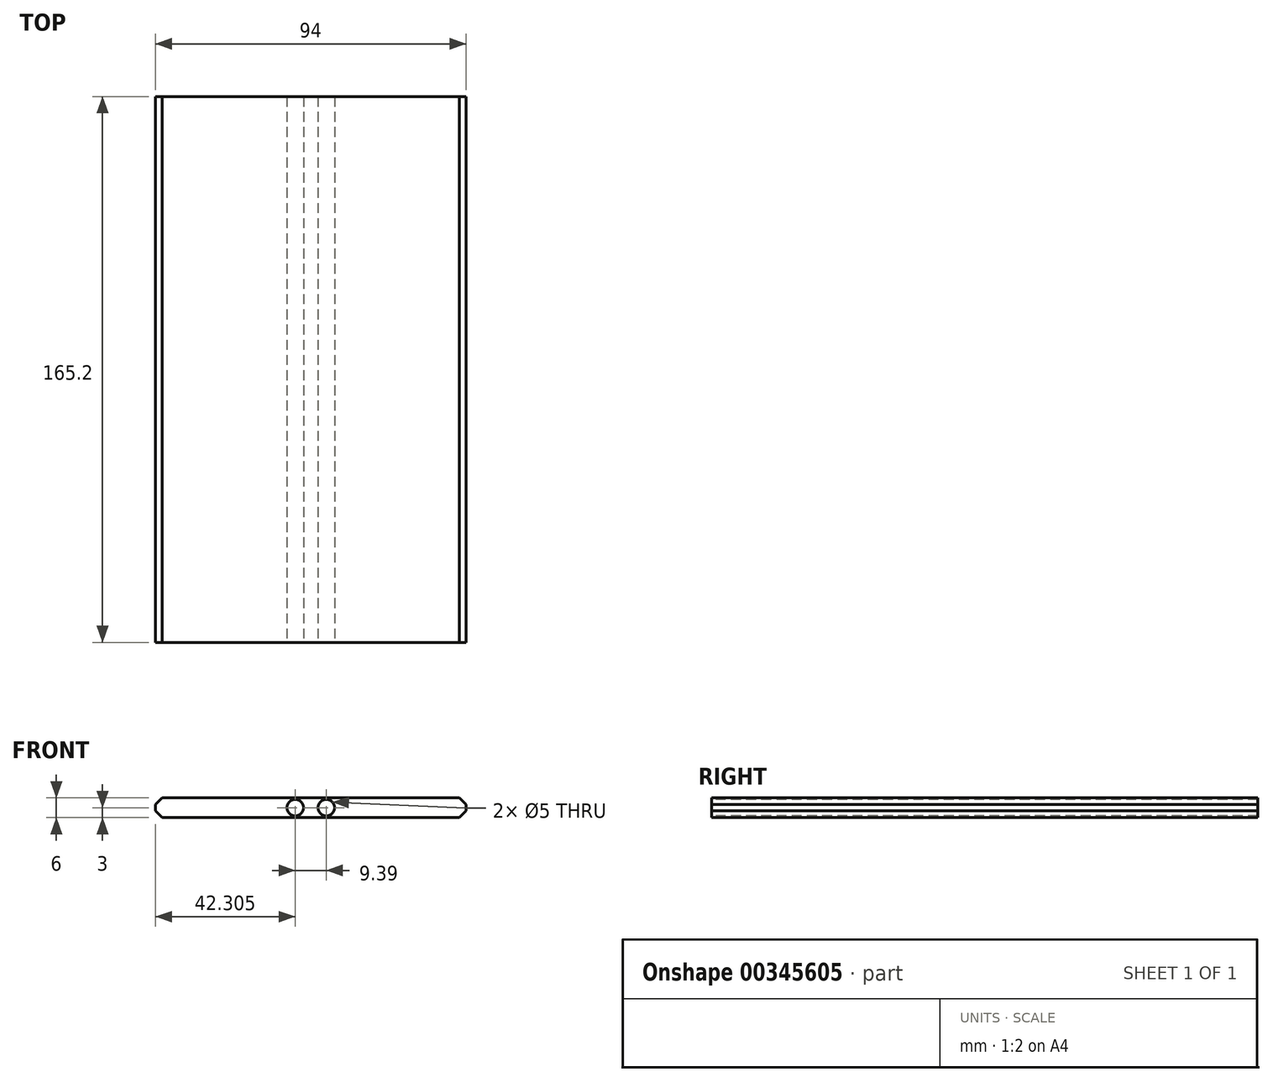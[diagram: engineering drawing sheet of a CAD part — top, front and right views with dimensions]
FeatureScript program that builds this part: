
annotation { "Feature Type Name" : "Feature", "Feature Type Description" : "" }
export const myFeature = defineFeature(function(context is Context, id is Id, definition is map)
    precondition{}
    {
        {
            var Q0;
            Q0=qCreatedBy(makeId("Top.planeOp"),FACE);
            var sketch = newSketch(context, id + "F0", { "sketchPlane" : qUnion([Q0])});
            skLineSegment(sketch, "E0.bottom", {"start": v(0, 0) * mm, "end": v(94, 0) * mm});
            skLineSegment(sketch, "E0.top", {"start": v(0, 165.2) * mm, "end": v(94, 165.2) * mm});
            skLineSegment(sketch, "E0.left", {"start": v(0, 0) * mm, "end": v(0, 165.2) * mm});
            skLineSegment(sketch, "E0.right", {"start": v(94, 0) * mm, "end": v(94, 165.2) * mm});
            skSolve(sketch);
        }
        {
            var Q0;
            Q0=makeQuery(id+"F0.imprint","IMPRINT",FACE,{"disambiguationData":[TD([[makeQuery(id+"F0.imprint","IMPRINT",EDGE,{"derivedFrom":sQuery(id+"F0.wireOp",EDGE,"E0.bottom")}),1.0]])]});
            extrude(context, id + "F1", {"entities" : qUnion([Q0]), "depth" : 6 * mm});
        }
        {
            var Q0;
            Q0=makeQuery(id+"F1.opExtrude","SWEPT_FACE",FACE,{"disambiguationData":[OSD([sQuery(id+"F0.wireOp",EDGE,"E0.bottom")])]});
            var sketch = newSketch(context, id + "F2", { "sketchPlane" : qUnion([Q0])});
            skCircle(sketch, "E1", {"center": v(42.3, 3) * mm, "radius": 2.5 * mm});
            skCircle(sketch, "E2", {"center": v(51.7, 3) * mm, "radius": 2.5 * mm});
            skLineSegment(sketch, "E3", {"start": v(47, 0) * mm, "end": v(47, 6) * mm});
            skPoint(sketch, "E3.endSnap0", {"position": v(47, 6) * mm});
            skSolve(sketch);
        }
        {
            var Q0;
            Q0=makeQuery(id+"F2.imprint","IMPRINT",FACE,{"disambiguationData":[TD([[makeQuery(id+"F2.imprint","IMPRINT",EDGE,{"derivedFrom":sQuery(id+"F2.wireOp",EDGE,"E1")}),1.0]])]});
            var Q1;
            Q1=makeQuery(id+"F2.imprint","IMPRINT",FACE,{"disambiguationData":[TD([[makeQuery(id+"F2.imprint","IMPRINT",EDGE,{"derivedFrom":sQuery(id+"F2.wireOp",EDGE,"E2")}),1.0]])]});
            extrude(context, id + "F3", {"entities" : qUnion([Q0, Q1]), "operationType" : NewBodyOperationType.REMOVE, "endBound" : BoundingType.THROUGH_ALL, "oppositeDirection" : true, "depth" : 25 * mm});
        }
        {
            var Q0;
            Q0=makeQuery(id+"F1.opExtrude","CAP_EDGE",EDGE,{"disambiguationData":[OSD([sQuery(id+"F0.wireOp",EDGE,"E0.left")])],"isStart":false});
            var Q1;
            Q1=makeQuery(id+"F1.opExtrude","CAP_EDGE",EDGE,{"disambiguationData":[OSD([sQuery(id+"F0.wireOp",EDGE,"E0.left")])],"isStart":true});
            var Q2;
            Q2=makeQuery(id+"F1.opExtrude","CAP_EDGE",EDGE,{"disambiguationData":[OSD([sQuery(id+"F0.wireOp",EDGE,"E0.right")])],"isStart":false});
            var Q3;
            Q3=makeQuery(id+"F1.opExtrude","CAP_EDGE",EDGE,{"disambiguationData":[OSD([sQuery(id+"F0.wireOp",EDGE,"E0.right")])],"isStart":true});
            chamfer(context, id + "F4", {"entities" : qUnion([Q0, Q1, Q2, Q3]), "width" : 2 * mm, "tangentPropagation" : true});
        }
    });
